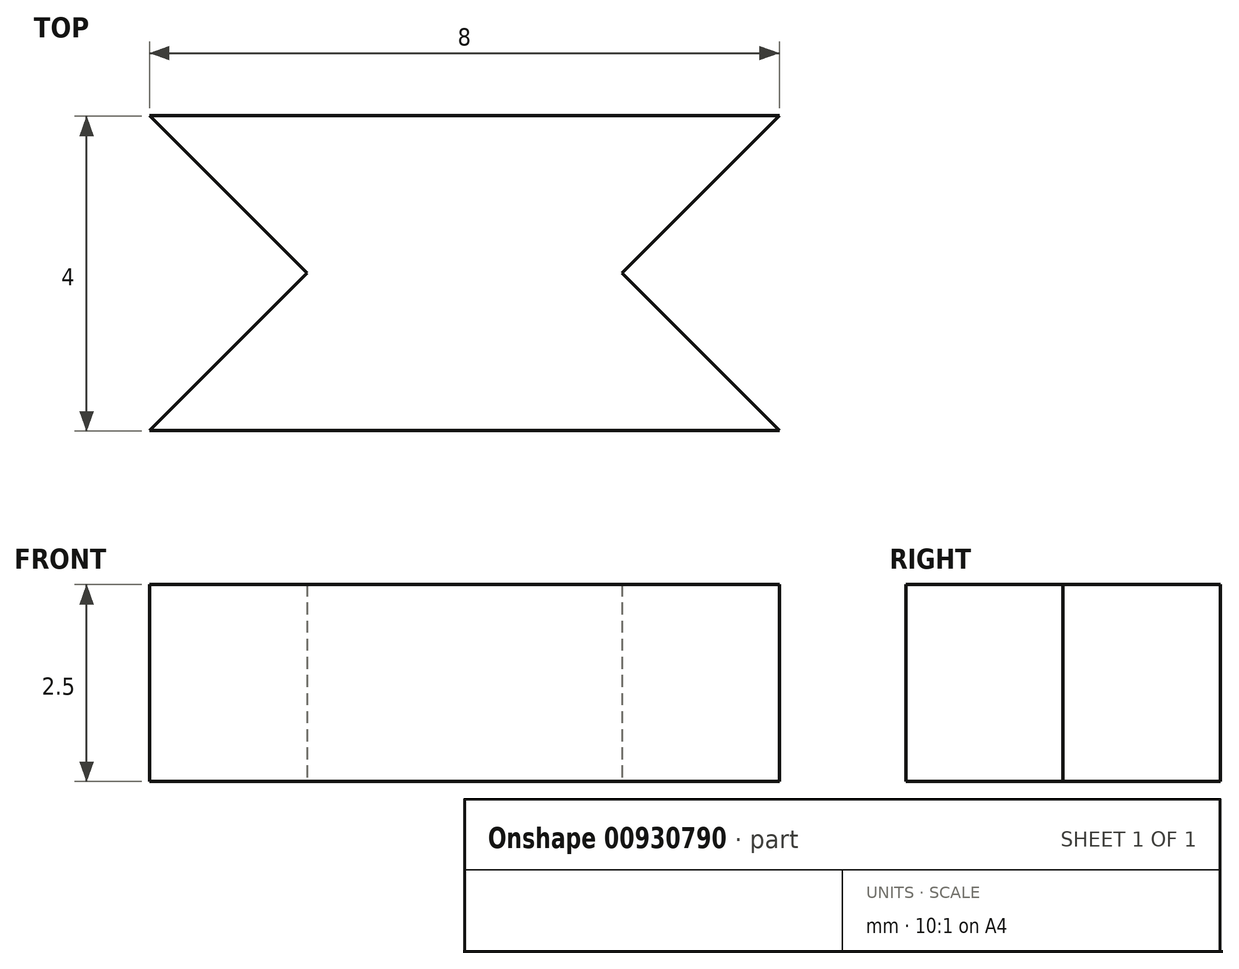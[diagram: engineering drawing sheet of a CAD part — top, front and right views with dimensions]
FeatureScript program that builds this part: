
annotation { "Feature Type Name" : "Feature", "Feature Type Description" : "" }
export const myFeature = defineFeature(function(context is Context, id is Id, definition is map)
    precondition{}
    {
        {
            var Q0;
            Q0=qCreatedBy(makeId("Top.planeOp"),FACE);
            var sketch = newSketch(context, id + "F0", { "sketchPlane" : qUnion([Q0])});
            skLineSegment(sketch, "E0", {"start": v(-6, -2.13) * mm, "end": v(2, -2.13) * mm});
            skLineSegment(sketch, "E1", {"start": v(2, -2.13) * mm, "end": v(0, -4.13) * mm});
            skLineSegment(sketch, "E2", {"start": v(0, -4.13) * mm, "end": v(2, -6.13) * mm});
            skLineSegment(sketch, "E3", {"start": v(2, -6.13) * mm, "end": v(-6, -6.13) * mm});
            skLineSegment(sketch, "E4", {"start": v(-6, -6.13) * mm, "end": v(-4, -4.13) * mm});
            skLineSegment(sketch, "E5", {"start": v(-4, -4.13) * mm, "end": v(-6, -2.13) * mm});
            skSolve(sketch);
        }
        {
            var Q0;
            Q0=makeQuery(id+"F0.imprint","IMPRINT",FACE,{"disambiguationData":[TD([[makeQuery(id+"F0.imprint","IMPRINT",EDGE,{"derivedFrom":sQuery(id+"F0.wireOp",EDGE,"E0")}),-1.0]])]});
            extrude(context, id + "F1", {"entities" : qUnion([Q0]), "depth" : 2.5 * mm, "offsetDistance" : 25 * mm});
        }
    });
